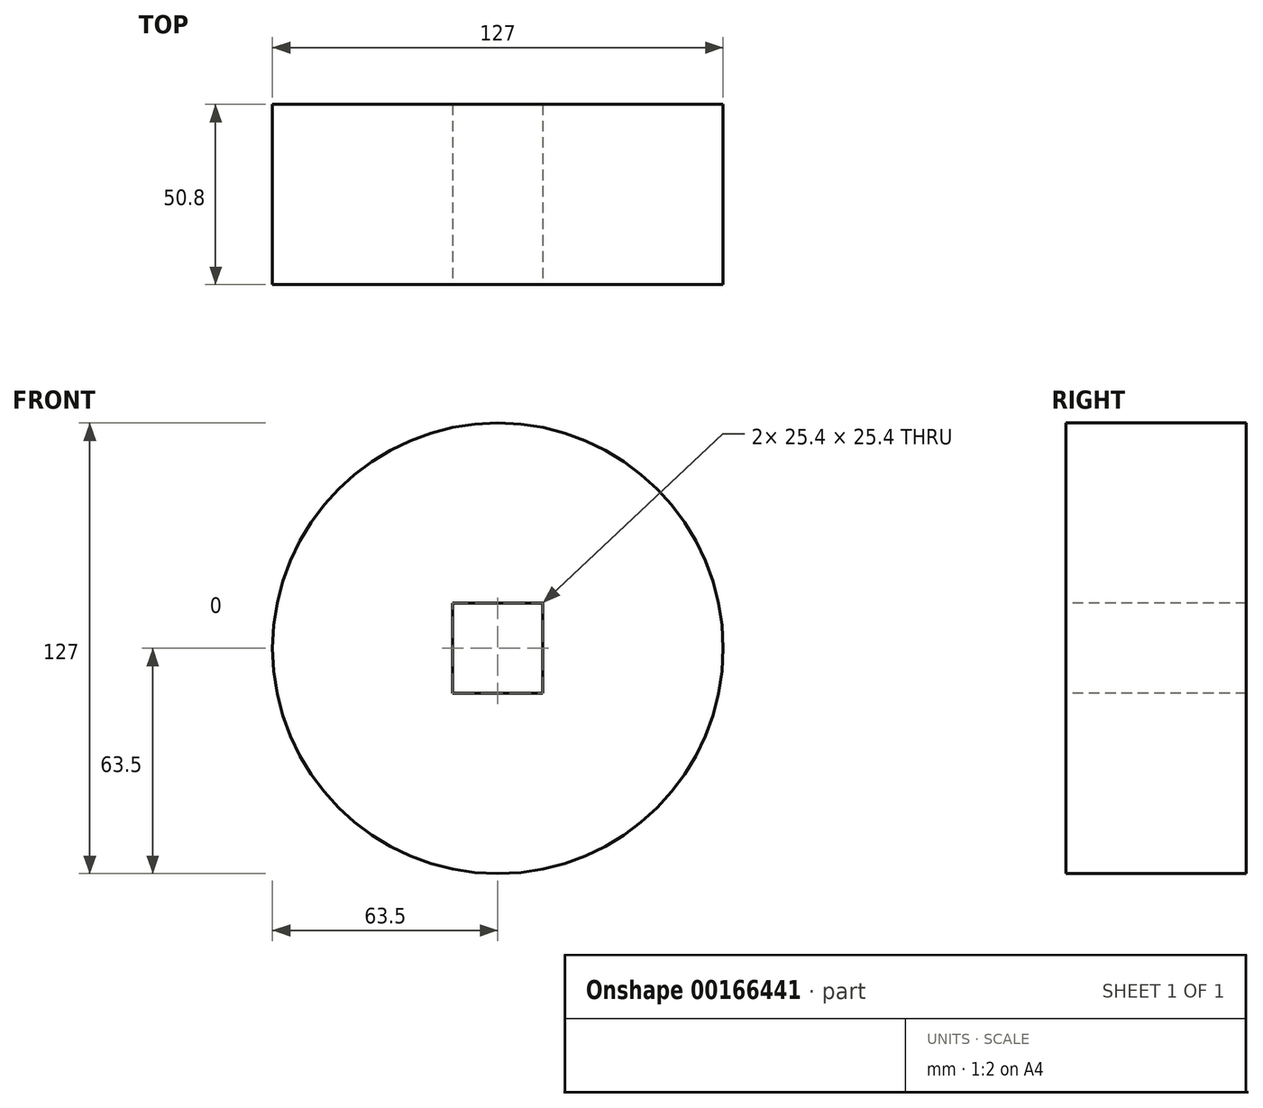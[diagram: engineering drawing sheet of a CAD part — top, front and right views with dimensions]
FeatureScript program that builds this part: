
annotation { "Feature Type Name" : "Feature", "Feature Type Description" : "" }
export const myFeature = defineFeature(function(context is Context, id is Id, definition is map)
    precondition{}
    {
        {
            var Q0;
            Q0=qCreatedBy(makeId("Front.planeOp"),FACE);
            var sketch = newSketch(context, id + "F0", { "sketchPlane" : qUnion([Q0])});
            skCircle(sketch, "E0", {"center": v(0, 0) * mm, "radius": 63.5 * mm});
            skSolve(sketch);
        }
        {
            var Q0;
            Q0 = qSketchRegion(id + "F0", true);
            var Q1;
            Q1=makeQuery(id+"F0.imprint","IMPRINT",FACE,{"disambiguationData":[TD([[makeQuery(id+"F0.imprint","IMPRINT",EDGE,{"derivedFrom":sQuery(id+"F0.wireOp",EDGE,"E0")}),1.0]])]});
            extrude(context, id + "F1", {"entities" : qUnion([Q0, Q1]), "endBound" : BoundingType.SYMMETRIC, "depth" : 50.8 * mm});
        }
        {
            var Q0;
            Q0=makeQuery(id+"F1.opExtrude","CAP_FACE",FACE,{"disambiguationData":[OSD([sQuery(id+"F0.wireOp",EDGE,"E0")])],"isStart":false});
            var sketch = newSketch(context, id + "F2", { "sketchPlane" : qUnion([Q0])});
            skLineSegment(sketch, "E1.bottom", {"start": v(12.7, 12.7) * mm, "end": v(-12.7, 12.7) * mm});
            skLineSegment(sketch, "E1.top", {"start": v(12.7, -12.7) * mm, "end": v(-12.7, -12.7) * mm});
            skLineSegment(sketch, "E1.left", {"start": v(12.7, 12.7) * mm, "end": v(12.7, -12.7) * mm});
            skLineSegment(sketch, "E1.right", {"start": v(-12.7, 12.7) * mm, "end": v(-12.7, -12.7) * mm});
            skPoint(sketch, "E1.middle", {"position": v(0, 0) * mm});
            skSolve(sketch);
        }
        {
            var Q0;
            Q0=makeQuery(id+"F2.imprint","IMPRINT",FACE,{"disambiguationData":[TD([[makeQuery(id+"F2.imprint","IMPRINT",EDGE,{"derivedFrom":sQuery(id+"F2.wireOp",EDGE,"E1.bottom")}),1.0]])]});
            extrude(context, id + "F3", {"entities" : qUnion([Q0]), "operationType" : NewBodyOperationType.REMOVE, "endBound" : BoundingType.THROUGH_ALL, "oppositeDirection" : true, "depth" : 25.4 * mm});
        }
    });
